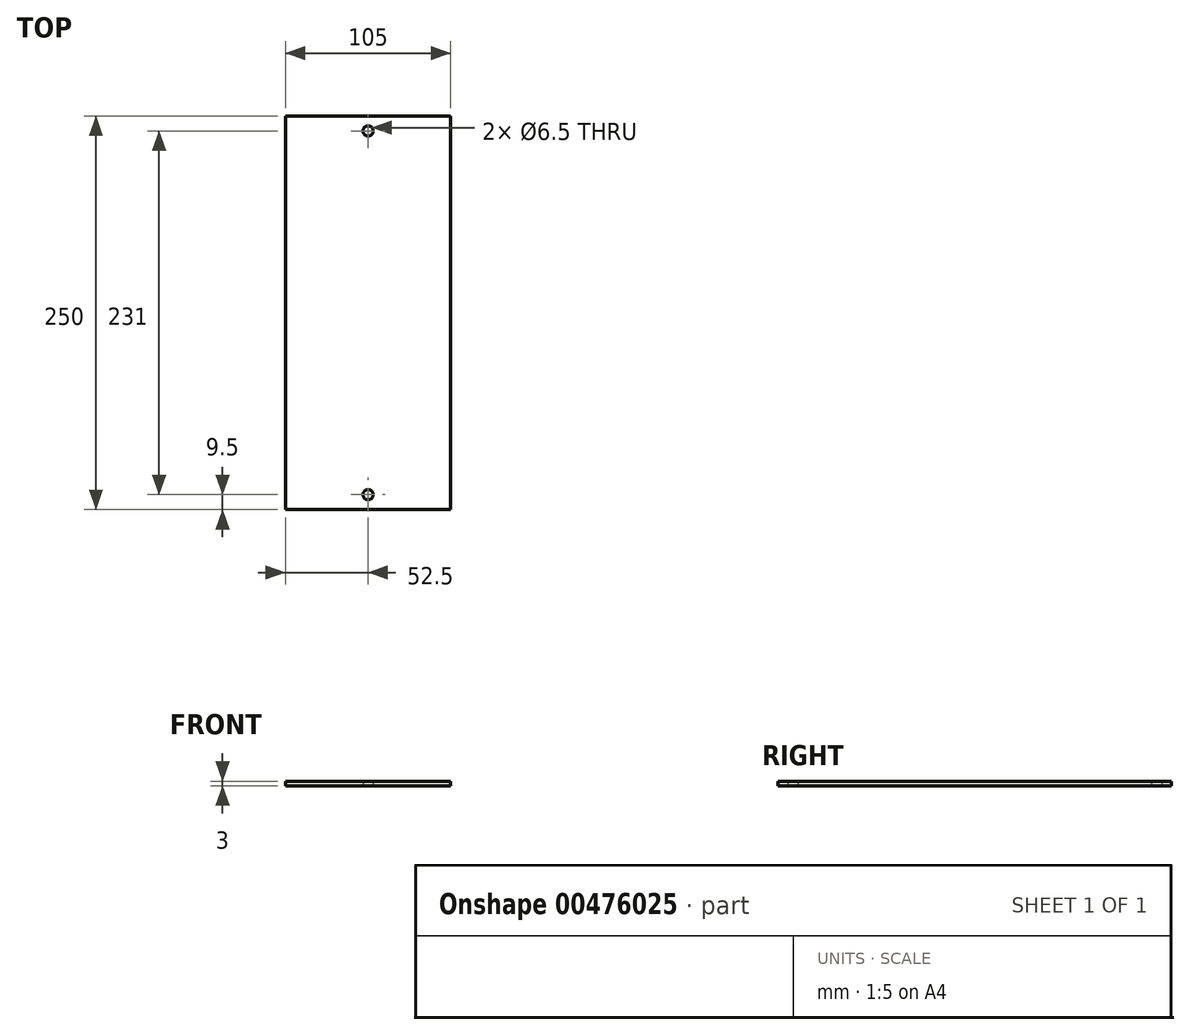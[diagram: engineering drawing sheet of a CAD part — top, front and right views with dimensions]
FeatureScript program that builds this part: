
annotation { "Feature Type Name" : "Feature", "Feature Type Description" : "" }
export const myFeature = defineFeature(function(context is Context, id is Id, definition is map)
    precondition{}
    {
        {
            var Q0;
            Q0=qCreatedBy(makeId("Top.planeOp"),FACE);
            var sketch = newSketch(context, id + "F0", { "sketchPlane" : qUnion([Q0])});
            skLineSegment(sketch, "E0.bottom", {"start": v(0, 0) * mm, "end": v(105, 0) * mm});
            skLineSegment(sketch, "E0.top", {"start": v(0, 250) * mm, "end": v(105, 250) * mm});
            skLineSegment(sketch, "E0.left", {"start": v(0, 0) * mm, "end": v(0, 250) * mm});
            skLineSegment(sketch, "E0.right", {"start": v(105, 0) * mm, "end": v(105, 250) * mm});
            skCircle(sketch, "E1", {"center": v(52.5, 240.5) * mm, "radius": 3.25 * mm});
            skLineSegment(sketch, "E2", {"start": v(0, 125) * mm, "end": v(105, 125) * mm});
            skCircle(sketch, "E3.MirrorC", {"center": v(52.5, 9.5) * mm, "radius": 3.25 * mm});
            skSolve(sketch);
        }
        {
            var Q0;
            Q0 = qSketchRegion(id + "F0", true);
            extrude(context, id + "F1", {"entities" : qUnion([Q0]), "depth" : 3 * mm});
        }
    });
